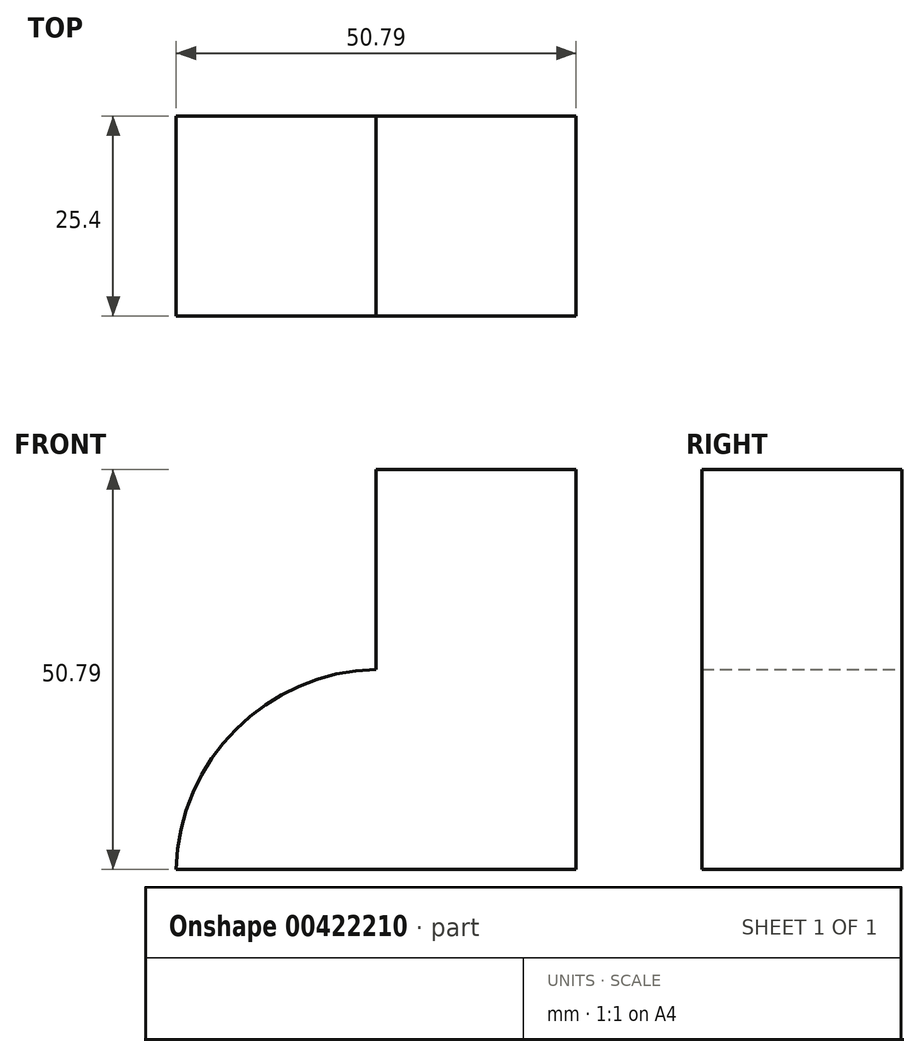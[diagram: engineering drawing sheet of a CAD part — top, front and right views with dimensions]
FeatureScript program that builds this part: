
annotation { "Feature Type Name" : "Feature", "Feature Type Description" : "" }
export const myFeature = defineFeature(function(context is Context, id is Id, definition is map)
    precondition{}
    {
        {
            var Q0;
            Q0=qCreatedBy(makeId("Front.planeOp"),FACE);
            var sketch = newSketch(context, id + "F0", { "sketchPlane" : qUnion([Q0])});
            skLineSegment(sketch, "E0", {"start": v(-71.99, 14.13) * mm, "end": v(-21.2, 14.13) * mm});
            skLineSegment(sketch, "E1", {"start": v(-21.2, 14.13) * mm, "end": v(-21.2, 64.92) * mm});
            skLineSegment(sketch, "E2", {"start": v(-21.2, 64.92) * mm, "end": v(-46.6, 64.92) * mm});
            skLineSegment(sketch, "E3", {"start": v(-46.6, 64.92) * mm, "end": v(-46.6, 39.53) * mm});
            skArc(sketch, "E4", {"start": v(-46.6, 39.53) * mm, "mid": v(-64.4, 31.94) * mm, "end": v(-71.99, 14.13) * mm});
            skSolve(sketch);
        }
        {
            var Q0;
            Q0=makeQuery(id+"F0.imprint","IMPRINT",FACE,{"disambiguationData":[TD([[makeQuery(id+"F0.imprint","IMPRINT",EDGE,{"derivedFrom":sQuery(id+"F0.wireOp",EDGE,"E0")}),1.0]])]});
            extrude(context, id + "F1", {"entities" : qUnion([Q0]), "depth" : 25.4 * mm});
        }
    });
